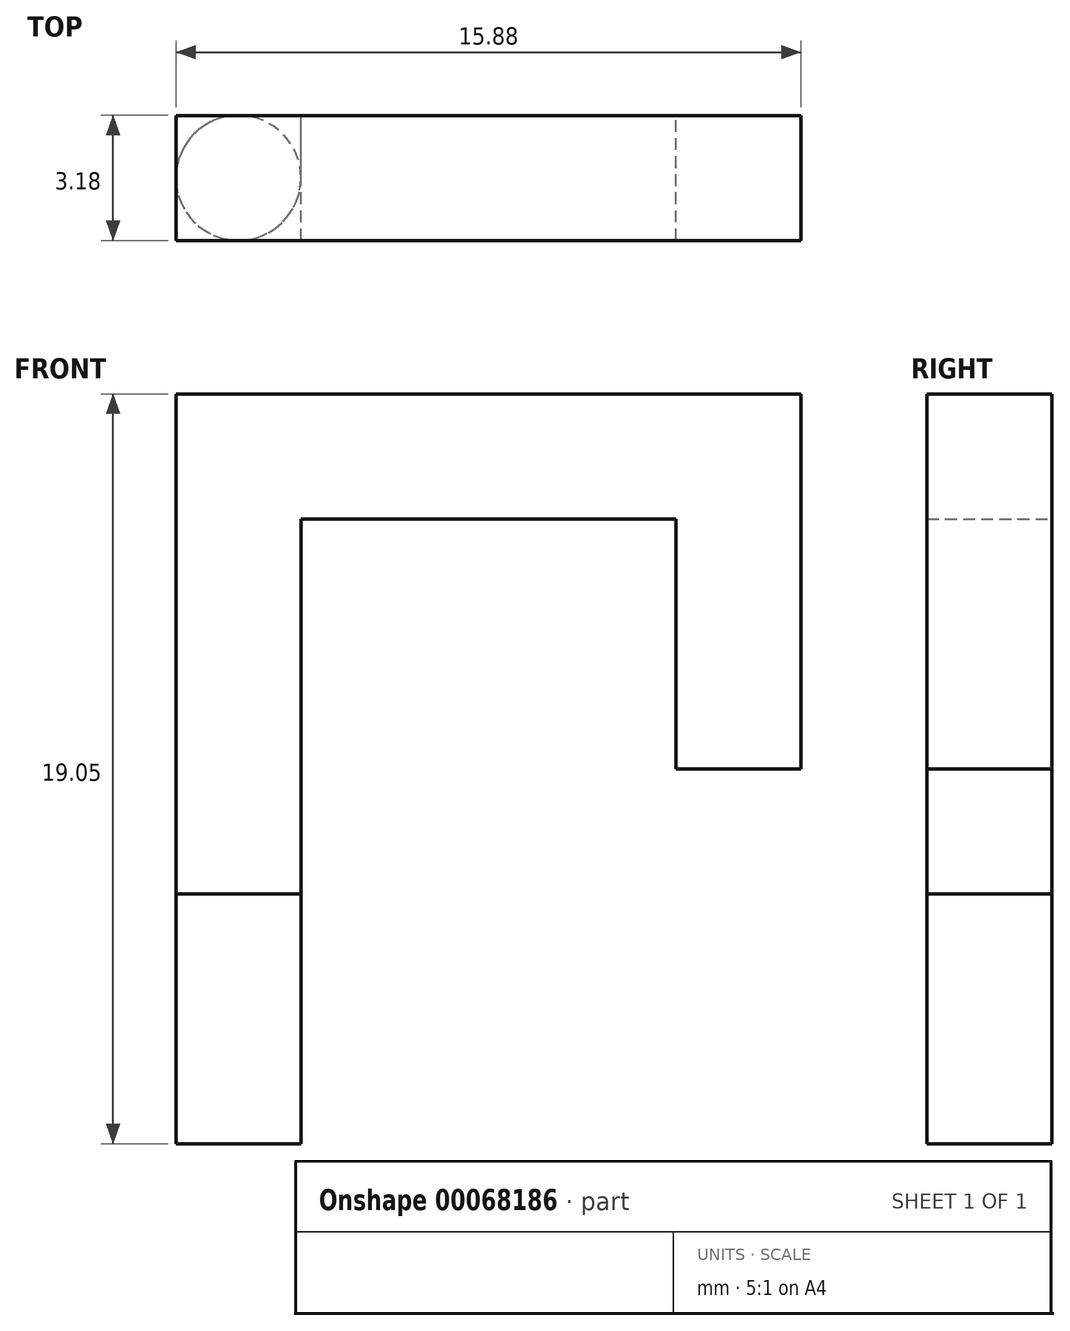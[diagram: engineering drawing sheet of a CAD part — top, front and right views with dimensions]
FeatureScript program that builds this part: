
annotation { "Feature Type Name" : "Feature", "Feature Type Description" : "" }
export const myFeature = defineFeature(function(context is Context, id is Id, definition is map)
    precondition{}
    {
        {
            var Q0;
            Q0=qCreatedBy(makeId("Top.planeOp"),FACE);
            var sketch = newSketch(context, id + "F0", { "sketchPlane" : qUnion([Q0])});
            skLineSegment(sketch, "E0.bottom", {"start": v(0, 0) * mm, "end": v(3.18, 0) * mm});
            skLineSegment(sketch, "E0.top", {"start": v(0, 3.17) * mm, "end": v(3.17, 3.17) * mm});
            skLineSegment(sketch, "E0.left", {"start": v(0, 0) * mm, "end": v(0, 3.17) * mm});
            skLineSegment(sketch, "E0.right", {"start": v(3.18, 0) * mm, "end": v(3.18, 3.17) * mm});
            skSolve(sketch);
        }
        {
            var Q0;
            Q0 = qSketchRegion(id + "F0", true);
            extrude(context, id + "F1", {"entities" : qUnion([Q0]), "depth" : 12.7 * mm});
        }
        {
            var Q0;
            Q0=makeQuery(id+"F1.opExtrude","SWEPT_FACE",FACE,{"disambiguationData":[OSD([sQuery(id+"F0.wireOp",EDGE,"E0.right")])]});
            var sketch = newSketch(context, id + "F2", { "sketchPlane" : qUnion([Q0])});
            skLineSegment(sketch, "E1.bottom", {"start": v(0, 12.7) * mm, "end": v(3.18, 12.7) * mm});
            skLineSegment(sketch, "E1.top", {"start": v(0, 9.53) * mm, "end": v(3.17, 9.53) * mm});
            skLineSegment(sketch, "E1.left", {"start": v(0, 12.7) * mm, "end": v(0, 9.53) * mm});
            skLineSegment(sketch, "E1.right", {"start": v(3.17, 12.7) * mm, "end": v(3.17, 9.53) * mm});
            skSolve(sketch);
        }
        {
            var Q0;
            Q0 = qSketchRegion(id + "F2", true);
            extrude(context, id + "F3", {"entities" : qUnion([Q0]), "operationType" : NewBodyOperationType.ADD, "depth" : 12.7 * mm});
        }
        {
            var Q0;
            Q0=makeQuery(id+"F3.opExtrude","SWEPT_FACE",FACE,{"disambiguationData":[OSD([sQuery(id+"F2.wireOp",EDGE,"E1.top")])]});
            var sketch = newSketch(context, id + "F4", { "sketchPlane" : qUnion([Q0])});
            skLineSegment(sketch, "E2.bottom", {"start": v(15.88, 0) * mm, "end": v(12.7, 0) * mm});
            skLineSegment(sketch, "E2.top", {"start": v(15.88, -3.17) * mm, "end": v(12.7, -3.17) * mm});
            skLineSegment(sketch, "E2.left", {"start": v(15.88, 0) * mm, "end": v(15.88, -3.17) * mm});
            skLineSegment(sketch, "E2.right", {"start": v(12.7, 0) * mm, "end": v(12.7, -3.17) * mm});
            skSolve(sketch);
        }
        {
            var Q0;
            Q0=makeQuery(id+"F4.imprint","IMPRINT",FACE,{"disambiguationData":[TD([[makeQuery(id+"F4.imprint","IMPRINT",EDGE,{"derivedFrom":sQuery(id+"F4.wireOp",EDGE,"E2.bottom")}),1.0]])]});
            extrude(context, id + "F5", {"entities" : qUnion([Q0]), "operationType" : NewBodyOperationType.ADD, "depth" : 6.35 * mm});
        }
        {
            var Q0;
            Q0=qCreatedBy(makeId("Top.planeOp"),FACE);
            var sketch = newSketch(context, id + "F6", { "sketchPlane" : qUnion([Q0])});
            skCircle(sketch, "E3", {"center": v(1.59, 1.59) * mm, "radius": 1.59 * mm});
            skSolve(sketch);
        }
        {
            var Q0;
            Q0 = qSketchRegion(id + "F6", true);
            extrude(context, id + "F7", {"entities" : qUnion([Q0]), "operationType" : NewBodyOperationType.ADD, "oppositeDirection" : true, "depth" : 6.35 * mm});
        }
    });
